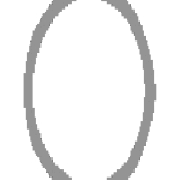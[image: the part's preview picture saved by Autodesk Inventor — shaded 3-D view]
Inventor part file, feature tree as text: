
AUTODESK INVENTOR PART (.ipt)
format: ipt  version: 2021 (Build 250183000, 183)  size: 113,152 bytes
history: native  units: in
note: dims shown in document units (in); Inventor stores cm internally (conversion verified against a paired STEP export)
features: other x4, sketch x3, plane x1
ambient origin geometry x8: Origin, YZ Plane, XZ Plane, XY Plane, X Axis, Y Axis, Z Axis, Center Point
bodies: Solid1 (feature_tree), Body (feature_tree)
feature tree (8):
  other  "Driven Length"
  other  "Frame Generator"
  other  "Start Plane"
  other  "End Plane"
  sketch  "Sketch"  dims[d2=11.6851in d4=-0.0in d5=11.6851in d6=0.12in d7=0.0in d8=90.0deg d9=11.6851in]
  sketch  "Sketch2"  dims[d0=1.0in]
  plane  "Work Plane3"
  sketch  "Sketch3"  dims[d1=0.065in]
